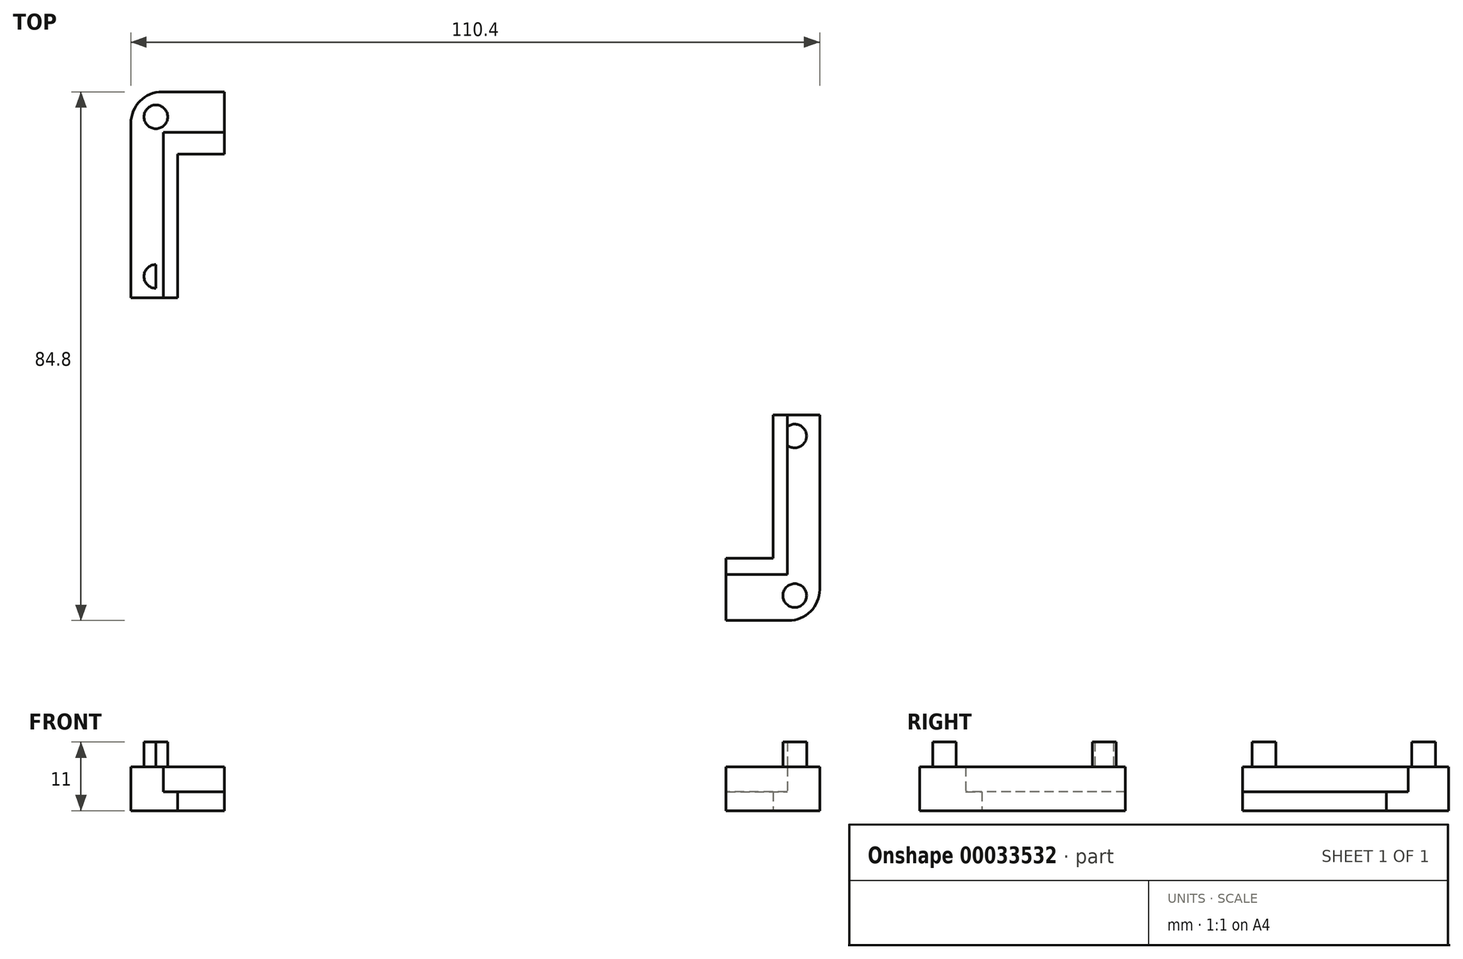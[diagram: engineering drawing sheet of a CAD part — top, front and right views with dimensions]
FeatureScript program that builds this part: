
annotation { "Feature Type Name" : "Feature", "Feature Type Description" : "" }
export const myFeature = defineFeature(function(context is Context, id is Id, definition is map)
    precondition{}
    {
        {
            var Q0;
            Q0=qCreatedBy(makeId("Top.planeOp"),FACE);
            var sketch = newSketch(context, id + "F0", { "sketchPlane" : qUnion([Q0])});
            skCircle(sketch, "E0", {"center": v(0, 0) * mm, "radius": 1.9 * mm});
            skLineSegment(sketch, "E1", {"start": v(0, -1.9) * mm, "end": v(0, -25.6) * mm});
            skCircle(sketch, "E2", {"center": v(0, -25.6) * mm, "radius": 1.9 * mm});
            skLineSegment(sketch, "E3", {"start": v(0, -25.6) * mm, "end": v(-6.95, -25.6) * mm});
            skLineSegment(sketch, "E4", {"start": v(1.9, 0) * mm, "end": v(25.6, 0) * mm});
            skLineSegment(sketch, "E5", {"start": v(25.6, 0) * mm, "end": v(25.6, 8.64) * mm});
            skCircle(sketch, "E6.MirrorC", {"center": v(51.2, 0) * mm, "radius": 1.9 * mm});
            skCircle(sketch, "E7.MirrorC", {"center": v(0, -51.2) * mm, "radius": 1.9 * mm});
            skLineSegment(sketch, "E8", {"start": v(0, -51.2) * mm, "end": v(-7.3, -51.2) * mm});
            skCircle(sketch, "E9.MirrorC", {"center": v(0, -76.8) * mm, "radius": 1.9 * mm});
            skLineSegment(sketch, "E10", {"start": v(51.2, 0) * mm, "end": v(51.2, 8.59) * mm});
            skCircle(sketch, "E11.MirrorC", {"center": v(102.4, 0) * mm, "radius": 1.9 * mm});
            skCircle(sketch, "E12.MirrorC", {"center": v(102.4, -76.8) * mm, "radius": 1.9 * mm});
            skLineSegment(sketch, "E13", {"start": v(0, -1.9) * mm, "end": v(0, -76.8) * mm});
            skLineSegment(sketch, "E14", {"start": v(1.9, 0) * mm, "end": v(102.4, 0) * mm});
            skLineSegment(sketch, "E15", {"start": v(4.23, 0) * mm, "end": v(4.23, -3.4) * mm});
            skLineSegment(sketch, "E16", {"start": v(102.4, 0) * mm, "end": v(102.4, -74.9) * mm});
            skPoint(sketch, "E17.start.orphan", {"position": v(102.4, -38.4) * mm});
            skLineSegment(sketch, "E18", {"start": v(100.5, -76.8) * mm, "end": v(0, -76.8) * mm});
            skPoint(sketch, "E19.start.orphan", {"position": v(51.2, -76.8) * mm});
            skLineSegment(sketch, "E20", {"start": v(51.2, -76.8) * mm, "end": v(51.2, -73.4) * mm});
            skPoint(sketch, "E21.start.orphan", {"position": v(98, -73.4) * mm});
            skLineSegment(sketch, "E22", {"start": v(51.2, -73.4) * mm, "end": v(101.2, -73.4) * mm});
            skLineSegment(sketch, "E23", {"start": v(101.2, -73.4) * mm, "end": v(101.2, -3.4) * mm});
            skLineSegment(sketch, "E24", {"start": v(101.2, -3.4) * mm, "end": v(1.2, -3.4) * mm});
            skLineSegment(sketch, "E25", {"start": v(51.2, -73.4) * mm, "end": v(1.2, -73.4) * mm});
            skLineSegment(sketch, "E26", {"start": v(1.2, -73.4) * mm, "end": v(1.2, -3.4) * mm});
            skCircle(sketch, "E27.MirrorC", {"center": v(102.4, -51.2) * mm, "radius": 1.9 * mm});
            skLineSegment(sketch, "E28", {"start": v(101.2, -65.25) * mm, "end": v(71.2, -65.25) * mm});
            skLineSegment(sketch, "E29", {"start": v(71.2, -73.4) * mm, "end": v(71.2, -53.4) * mm});
            skSolve(sketch);
        }
        {
            var Q0;
            Q0=qCreatedBy(makeId("Top.planeOp"),FACE);
            var sketch = newSketch(context, id + "F1", { "sketchPlane" : qUnion([Q0])});
            skLineSegment(sketch, "E30", {"start": v(0, 0) * mm, "end": v(0, 4) * mm});
            skLineSegment(sketch, "E31", {"start": v(0, 4) * mm, "end": v(-4, 4) * mm});
            skLineSegment(sketch, "E32", {"start": v(-4, 4) * mm, "end": v(-4, -6) * mm});
            skLineSegment(sketch, "E33", {"start": v(-4, -6) * mm, "end": v(1.21, -6) * mm});
            skLineSegment(sketch, "E34", {"start": v(3.5, -2.5) * mm, "end": v(3.5, 4.63) * mm});
            skLineSegment(sketch, "E35", {"start": v(0, 4) * mm, "end": v(3.5, 4) * mm});
            skLineSegment(sketch, "E36", {"start": v(1.21, -3.4) * mm, "end": v(1.21, -6) * mm});
            skLineSegment(sketch, "E37", {"start": v(106.4, -76.8) * mm, "end": v(106.4, -80.8) * mm});
            skLineSegment(sketch, "E38", {"start": v(106.4, -80.8) * mm, "end": v(98.9, -80.8) * mm});
            skLineSegment(sketch, "E39", {"start": v(106.4, -70.8) * mm, "end": v(106.4, -76.8) * mm});
            skLineSegment(sketch, "E40", {"start": v(101.2, -73.4) * mm, "end": v(98.9, -73.4) * mm});
            skLineSegment(sketch, "E41", {"start": v(101.2, -73.4) * mm, "end": v(101.2, -70.8) * mm});
            skLineSegment(sketch, "E42", {"start": v(-4, -6) * mm, "end": v(-4, -16) * mm});
            skLineSegment(sketch, "E43", {"start": v(-4, -16) * mm, "end": v(3.5, -16) * mm});
            skLineSegment(sketch, "E44", {"start": v(3.5, -16) * mm, "end": v(3.5, -6) * mm});
            skLineSegment(sketch, "E45", {"start": v(3.5, 4) * mm, "end": v(11, 4) * mm});
            skLineSegment(sketch, "E46", {"start": v(11, 4) * mm, "end": v(11, -6) * mm});
            skLineSegment(sketch, "E47", {"start": v(3.5, -6) * mm, "end": v(11, -6) * mm});
            skLineSegment(sketch, "E48", {"start": v(106.4, -70.8) * mm, "end": v(106.4, -60.8) * mm});
            skLineSegment(sketch, "E49", {"start": v(106.4, -60.8) * mm, "end": v(98.9, -60.8) * mm});
            skLineSegment(sketch, "E50", {"start": v(98.9, -60.8) * mm, "end": v(98.9, -70.8) * mm});
            skLineSegment(sketch, "E51", {"start": v(98.9, -80.8) * mm, "end": v(91.4, -80.8) * mm});
            skLineSegment(sketch, "E52", {"start": v(91.4, -80.8) * mm, "end": v(91.4, -70.8) * mm});
            skLineSegment(sketch, "E53", {"start": v(98.9, -70.8) * mm, "end": v(91.4, -70.8) * mm});
            skLineSegment(sketch, "E54", {"start": v(1.21, -6) * mm, "end": v(1.21, -16) * mm});
            skLineSegment(sketch, "E55", {"start": v(101.2, -70.8) * mm, "end": v(101.2, -60.8) * mm});
            skLineSegment(sketch, "E56", {"start": v(98.9, -73.4) * mm, "end": v(91.4, -73.4) * mm});
            skLineSegment(sketch, "E57", {"start": v(-4, -16) * mm, "end": v(-4, -29) * mm});
            skLineSegment(sketch, "E58", {"start": v(-4, -29) * mm, "end": v(3.5, -29) * mm});
            skLineSegment(sketch, "E59", {"start": v(3.5, -16) * mm, "end": v(3.5, -29) * mm});
            skLineSegment(sketch, "E60", {"start": v(106.4, -60.8) * mm, "end": v(106.4, -47.8) * mm});
            skLineSegment(sketch, "E61", {"start": v(106.4, -47.8) * mm, "end": v(98.9, -47.8) * mm});
            skLineSegment(sketch, "E62", {"start": v(98.9, -60.8) * mm, "end": v(98.9, -47.8) * mm});
            skLineSegment(sketch, "E63", {"start": v(101.2, -60.8) * mm, "end": v(101.2, -47.8) * mm});
            skLineSegment(sketch, "E64", {"start": v(1.21, -16) * mm, "end": v(1.21, -29) * mm});
            skLineSegment(sketch, "E65", {"start": v(11, -2.5) * mm, "end": v(3.5, -2.5) * mm});
            skPoint(sketch, "E66.end.orphan", {"position": v(7.25, -2.5) * mm});
            skPoint(sketch, "E66.start.orphan", {"position": v(7.25, 4) * mm});
            skLineSegment(sketch, "E67", {"start": v(3.5, -2.5) * mm, "end": v(1.21, -2.5) * mm});
            skLineSegment(sketch, "E68", {"start": v(1.21, -2.5) * mm, "end": v(1.21, -3.4) * mm});
            skLineSegment(sketch, "E69", {"start": v(3.5, -6) * mm, "end": v(1.21, -6) * mm});
            skSolve(sketch);
        }
        {
            var Q0;
            Q0 = qSketchRegion(id + "F1", true);
            extrude(context, id + "F2", {"entities" : qUnion([Q0]), "depth" : 3 * mm});
        }
        {
            var Q0;
            Q0=makeQuery(id+"F1.imprint","IMPRINT",FACE,{"disambiguationData":[TD([[makeQuery(id+"F1.imprint","IMPRINT",EDGE,{"derivedFrom":sQuery(id+"F1.wireOp",EDGE,"E33")}),-1.0]])]});
            var Q1;
            {var subQ2=sQuery(id+"F1.wireOp",EDGE,"E45");Q1=makeQuery(id+"F1.imprint","IMPRINT",FACE,{"disambiguationData":[TD([[makeQuery(id+"F1.imprint","IMPRINT",EDGE,{"derivedFrom":subQ2}),-1.0]])]});}
            var Q2;
            Q2=makeQuery(id+"F1.imprint","IMPRINT",FACE,{"disambiguationData":[TD([[makeQuery(id+"F1.imprint","IMPRINT",EDGE,{"derivedFrom":sQuery(id+"F1.wireOp",EDGE,"E31")}),1.0]])]});
            var Q3;
            Q3=makeQuery(id+"F1.imprint","IMPRINT",FACE,{"disambiguationData":[TD([[makeQuery(id+"F1.imprint","IMPRINT",EDGE,{"derivedFrom":sQuery(id+"F1.wireOp",EDGE,"E37")}),-1.0]])]});
            var Q4;
            {var subQ2=sQuery(id+"F1.wireOp",EDGE,"E57");Q4=makeQuery(id+"F1.imprint","IMPRINT",FACE,{"disambiguationData":[TD([[makeQuery(id+"F1.imprint","IMPRINT",EDGE,{"derivedFrom":subQ2}),1.0]])]});}
            var Q5;
            {var subQ2=sQuery(id+"F1.wireOp",EDGE,"E60");Q5=makeQuery(id+"F1.imprint","IMPRINT",FACE,{"disambiguationData":[TD([[makeQuery(id+"F1.imprint","IMPRINT",EDGE,{"derivedFrom":subQ2}),1.0]])]});}
            extrude(context, id + "F3", {"entities" : qUnion([Q0, Q1, Q2, Q3, Q4, Q5]), "operationType" : NewBodyOperationType.ADD, "depth" : 7 * mm});
        }
        {
            var Q0;
            {var subQ0=sQuery(id+"F0.wireOp",EDGE,"E0");var subQ2=makeQuery(id+"F0.imprint","INTERSECT",VERTEX,{"derivedFrom":[subQ0,sQuery(id+"F0.wireOp",EDGE,"E13")]});Q0=makeQuery(id+"F0.imprint","IMPRINT",FACE,{"disambiguationData":[TD([[makeQuery(id+"F0.imprint","IMPRINT",EDGE,{"disambiguationData":[TD([[subQ2,1.0]])],"derivedFrom":subQ0}),1.0]])]});}
            var Q1;
            {var subQ0=sQuery(id+"F0.wireOp",EDGE,"E12.MirrorC");var subQ2=makeQuery(id+"F0.imprint","INTERSECT",VERTEX,{"derivedFrom":[subQ0,sQuery(id+"F0.wireOp",EDGE,"E16")]});Q1=makeQuery(id+"F0.imprint","IMPRINT",FACE,{"disambiguationData":[TD([[makeQuery(id+"F0.imprint","IMPRINT",EDGE,{"disambiguationData":[TD([[subQ2,1.0]])],"derivedFrom":subQ0}),1.0]])]});}
            var Q2;
            {var subQ0=sQuery(id+"F0.wireOp",EDGE,"E27.MirrorC");var subQ1=sQuery(id+"F0.wireOp",EDGE,"E16");var subQ3=makeQuery(id+"F0.imprint","INTERSECT",VERTEX,{"disambiguationData":[OD(0.0)],"derivedFrom":[subQ1,subQ0]});Q2=makeQuery(id+"F0.imprint","IMPRINT",FACE,{"disambiguationData":[TD([[makeQuery(id+"F0.imprint","IMPRINT",EDGE,{"disambiguationData":[TD([[subQ3,-1.0]])],"derivedFrom":subQ1}),1.0]])]});}
            var Q3;
            {var subQ0=sQuery(id+"F0.wireOp",EDGE,"E27.MirrorC");var subQ3=sQuery(id+"F0.wireOp",EDGE,"E16");var subQ4=makeQuery(id+"F0.imprint","INTERSECT",VERTEX,{"disambiguationData":[OD(0.0)],"derivedFrom":[subQ3,subQ0]});Q3=makeQuery(id+"F0.imprint","IMPRINT",FACE,{"disambiguationData":[TD([[makeQuery(id+"F0.imprint","IMPRINT",EDGE,{"disambiguationData":[TD([[subQ4,-1.0]])],"derivedFrom":subQ3}),-1.0]])]});}
            var Q4;
            {var subQ1=sQuery(id+"F0.wireOp",EDGE,"E2");var subQ4=sQuery(id+"F0.wireOp",EDGE,"E13");var subQ7=makeQuery(id+"F0.imprint","INTERSECT",VERTEX,{"disambiguationData":[OD(0.0)],"derivedFrom":[subQ1,subQ4]});Q4=makeQuery(id+"F0.imprint","IMPRINT",FACE,{"disambiguationData":[TD([[makeQuery(id+"F0.imprint","IMPRINT",EDGE,{"disambiguationData":[TD([[subQ7,1.0]])],"derivedFrom":subQ1}),1.0]])]});}
            var Q5;
            {var subQ1=sQuery(id+"F0.wireOp",EDGE,"E2");var subQ3=sQuery(id+"F0.wireOp",EDGE,"E3");var subQ5=makeQuery(id+"F0.imprint","INTERSECT",VERTEX,{"derivedFrom":[subQ1,subQ3]});Q5=makeQuery(id+"F0.imprint","IMPRINT",FACE,{"disambiguationData":[TD([[makeQuery(id+"F0.imprint","IMPRINT",EDGE,{"disambiguationData":[TD([[subQ5,1.0]])],"derivedFrom":subQ1}),1.0]])]});}
            var Q6;
            {var subQ1=sQuery(id+"F0.wireOp",EDGE,"E2");var subQ3=sQuery(id+"F0.wireOp",EDGE,"E3");var subQ5=makeQuery(id+"F0.imprint","INTERSECT",VERTEX,{"derivedFrom":[subQ1,subQ3]});Q6=makeQuery(id+"F0.imprint","IMPRINT",FACE,{"disambiguationData":[TD([[makeQuery(id+"F0.imprint","IMPRINT",EDGE,{"disambiguationData":[TD([[subQ5,-1.0]])],"derivedFrom":subQ1}),1.0]])]});}
            extrude(context, id + "F4", {"entities" : qUnion([Q0, Q1, Q2, Q3, Q4, Q5, Q6]), "operationType" : NewBodyOperationType.ADD, "depth" : 11 * mm});
        }
        {
            var Q0;
            Q0=makeQuery(id+"F3.opExtrude","SWEPT_EDGE",EDGE,{"disambiguationData":[OSD([sQuery(id+"F1.wireOp",EDGE,"E31"),sQuery(id+"F1.wireOp",EDGE,"E32")])]});
            var Q1;
            Q1=makeQuery(id+"F3.opExtrude","SWEPT_EDGE",EDGE,{"disambiguationData":[OSD([sQuery(id+"F1.wireOp",EDGE,"E37"),sQuery(id+"F1.wireOp",EDGE,"E38")])]});
            var Q2;
            Q2=makeQuery(id+"F2.opExtrude","SWEPT_EDGE",EDGE,{"disambiguationData":[OSD([sQuery(id+"F1.wireOp",EDGE,"E37"),sQuery(id+"F1.wireOp",EDGE,"E38")])]});
            var Q3;
            Q3=makeQuery(id+"F2.opExtrude","SWEPT_EDGE",EDGE,{"disambiguationData":[OSD([sQuery(id+"F1.wireOp",EDGE,"E31"),sQuery(id+"F1.wireOp",EDGE,"E32")])]});
            fillet(context, id + "F5", {"entities" : qUnion([Q0, Q1, Q2, Q3]), "radius" : 5 * mm, "tangentPropagation" : true, "allowEdgeOverflow" : false});
        }
    });
